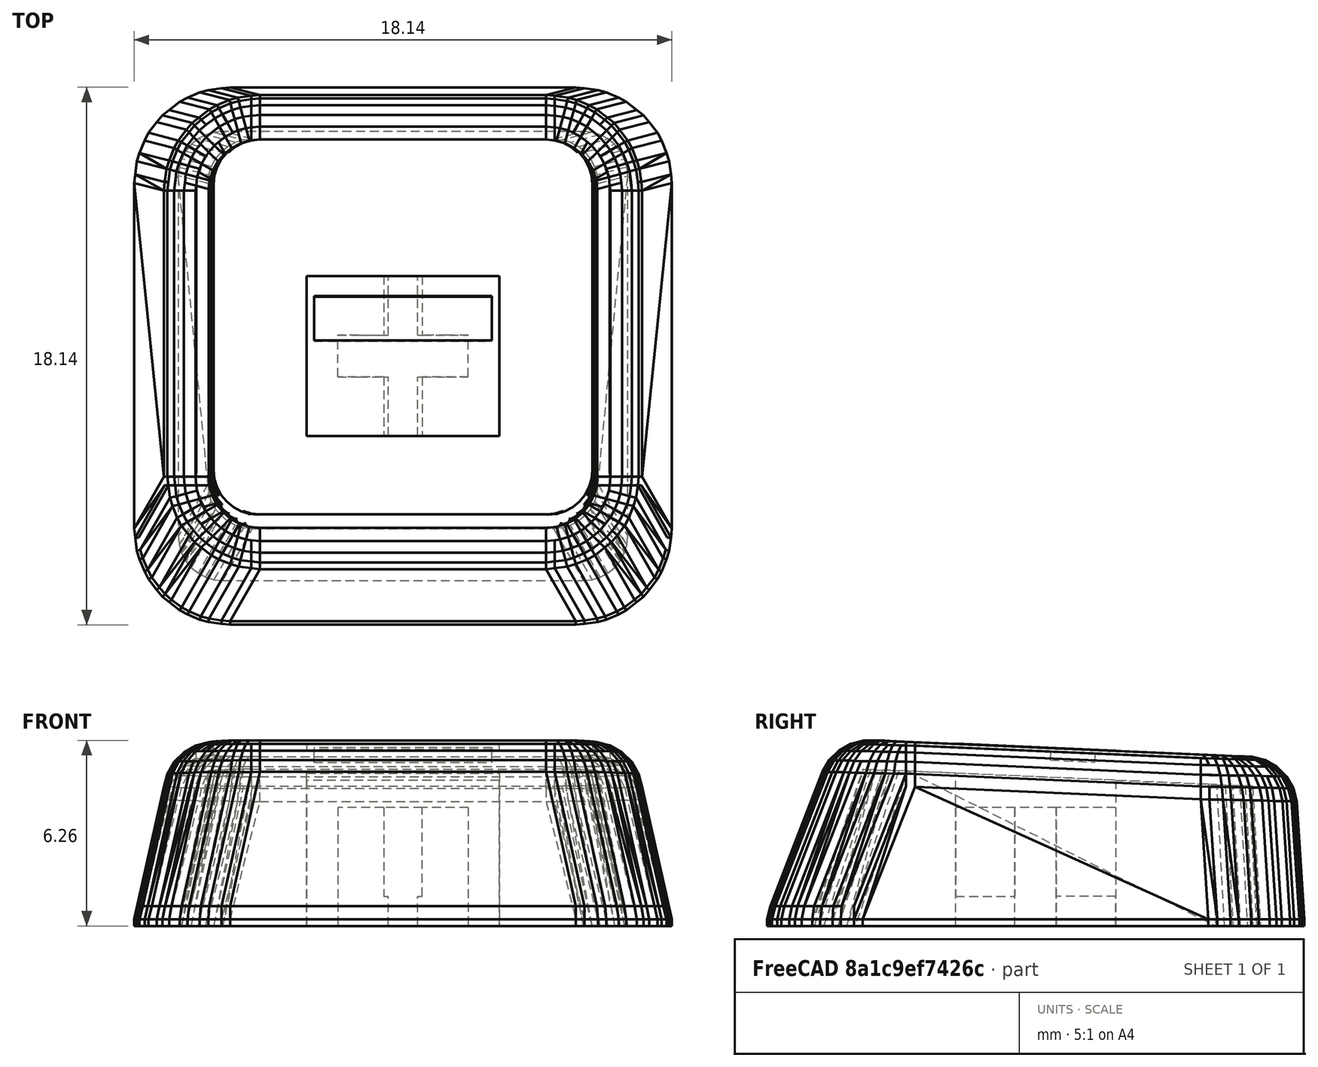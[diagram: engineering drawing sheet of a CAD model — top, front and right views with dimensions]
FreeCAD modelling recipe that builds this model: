
FCSTD DOCUMENT  (FreeCAD 0.18R16131 (Git))
Label: minus
License: All rights reserved
LicenseURL: http://en.wikipedia.org/wiki/All_rights_reserved
objects: Part::Box×5, Part::Feature×1, Part::MultiFuse×1, Part::Cut×1
note: 8 computed .brp shape members not serialized (recipe doc carries the construction recipe); baked Part::Feature solids carry a one-line shape summary decoded from their .brp

FEATURE [Part::Feature] Solid
  shape: bbox 18.13 x 18.13 x 6.262 mm, 1259 faces (baked)
FEATURE [Part::Box] Box  label="Cube"
  AttacherType = Attacher::AttachEngine3D
  Height = 1
  Length = 1
  Placement = pos=(0.5,-2.7,0) rot=(0,0,1;0rad)
  Width = 2
FEATURE [Part::Box] Box001  label="Cube001"
  AttacherType = Attacher::AttachEngine3D
  Height = 1
  Length = 1
  Placement = pos=(-1.5,0.7,0) rot=(0,0,1;0rad)
  Width = 2
FEATURE [Part::Box] Box002  label="Cube002"
  AttacherType = Attacher::AttachEngine3D
  Height = 1
  Length = 1
  Placement = pos=(-1.5,-2.7,0) rot=(0,0,1;0rad)
  Width = 2
FEATURE [Part::Box] Box003  label="Cube003"
  AttacherType = Attacher::AttachEngine3D
  Height = 1
  Length = 1
  Placement = pos=(0.5,0.7,0) rot=(0,0,1;0rad)
  Width = 2
FEATURE [Part::MultiFuse] Fusion
  Shapes = -> [Solid,Box002,Box001,Box,Box003]
FEATURE [Part::Box] Box004  label="Cube004"
  AttacherType = Attacher::AttachEngine3D
  Height = 0.5
  Length = 6
  Placement = pos=(-3,0.5,5.6) rot=(1,0,0;-0.05236rad)
  Width = 1.5
FEATURE [Part::Cut] Cut
  Base = -> Fusion
  Tool = -> Box004
